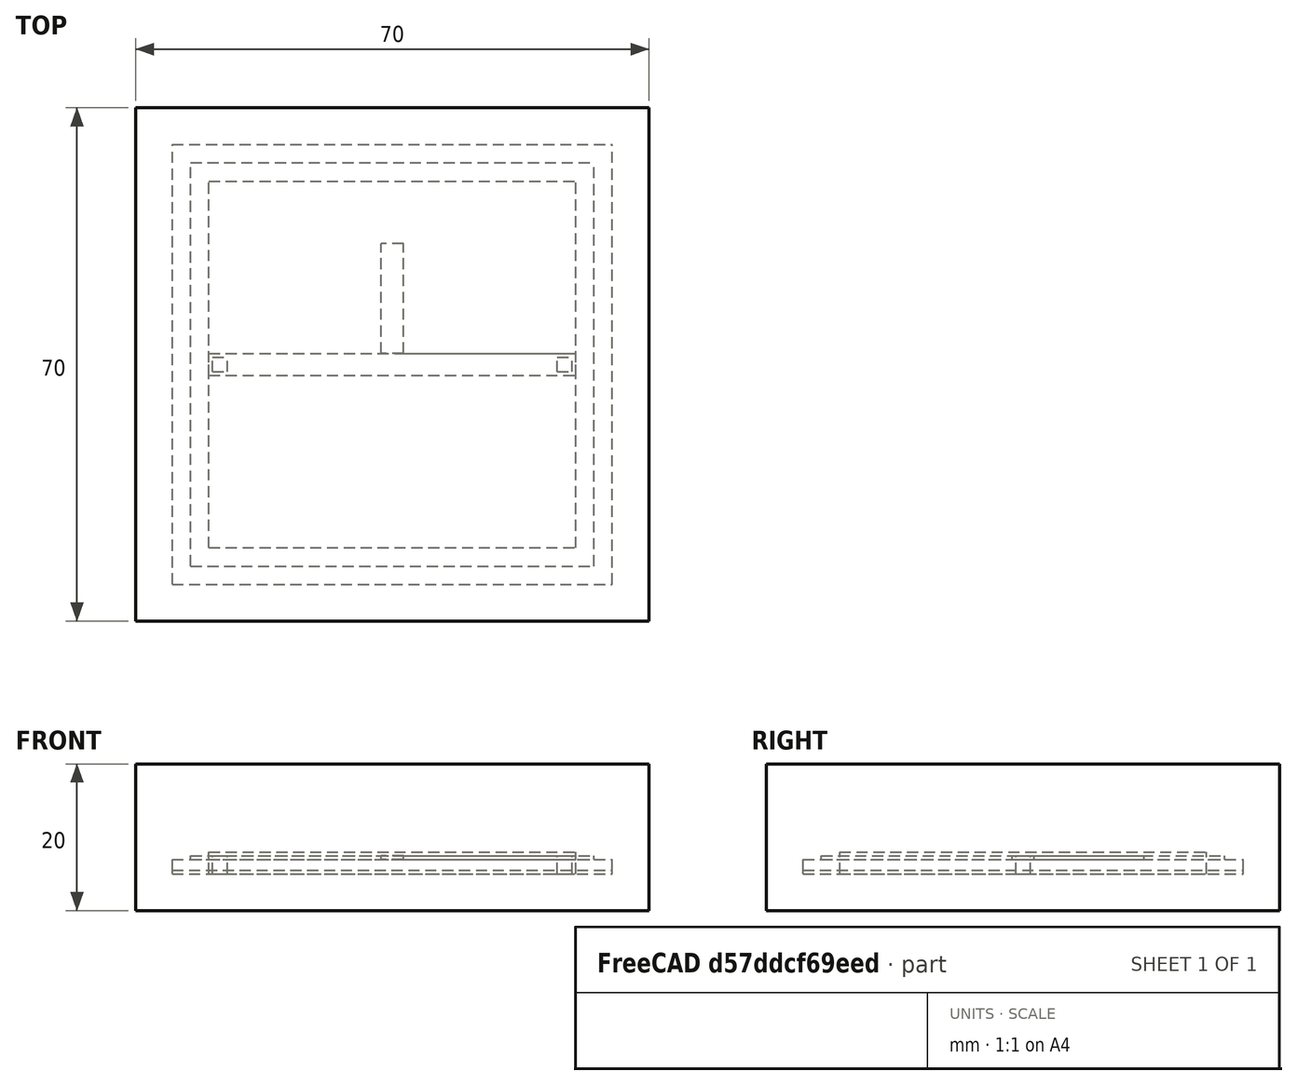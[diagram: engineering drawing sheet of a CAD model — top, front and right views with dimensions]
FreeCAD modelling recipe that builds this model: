
FCSTD DOCUMENT  (FreeCAD 0.21R29450 (Git))
Label: 002
License: All rights reserved
LicenseURL: http://en.wikipedia.org/wiki/All_rights_reserved
objects: Part::Box×9, PartDesign::Boolean×1, PartDesign::Body×1
note: 11 computed .brp shape members not serialized (recipe doc carries the construction recipe); baked Part::Feature solids carry a one-line shape summary decoded from their .brp

FEATURE [Part::Box] Box  label="Substrate"
  AttacherType = Attacher::AttachEngine3D
  Height = 1.5
  Length = 60
  Placement = pos=(-5,-5,0.5) rot=(0,0,1;0rad)
  Width = 60
FEATURE [Part::Box] Box001  label="GND"
  AttacherType = Attacher::AttachEngine3D
  Height = 0.5
  Length = 60
  Placement = pos=(-5,-5,0) rot=(0,0,1;0rad)
  Width = 60
FEATURE [Part::Box] Box002  label="Trace1"
  AttacherType = Attacher::AttachEngine3D
  Height = 0.5
  Length = 50
  Placement = pos=(0,23.5,2) rot=(0,0,1;0rad)
  Width = 3
FEATURE [Part::Box] Box003  label="Stub1"
  AttacherType = Attacher::AttachEngine3D
  Height = 0.5
  Length = 15
  Placement = pos=(26.5,26.5,2) rot=(0,0,1;1.5708rad)
  Width = 3
FEATURE [PartDesign::Boolean] Boolean
  Group = -> [Box002,Box003]
  Type = 0
FEATURE [PartDesign::Body] Body  label="Top_Conductor"
  Group = -> [Boolean]
  Origin = -> Origin
  Tip = -> Boolean
FEATURE [Part::Box] Box004  label="Term_IN"
  AttacherType = Attacher::AttachEngine3D
  Height = 2.5
  Length = 2
  Placement = pos=(0.5,24,0) rot=(0,0,1;0rad)
  Width = 2
FEATURE [Part::Box] Box005  label="Term_OUT"
  AttacherType = Attacher::AttachEngine3D
  Height = 2.5
  Length = 2
  Placement = pos=(47.5,24,0) rot=(0,0,1;0rad)
  Width = 2
FEATURE [Part::Box] Box006  label="Air_Volume"
  AttacherType = Attacher::AttachEngine3D
  Height = 20
  Length = 70
  Placement = pos=(-10,-10,-5) rot=(0,0,1;0rad)
  Width = 70
FEATURE [Part::Box] Box007  label="electric field port"
  AttacherType = Attacher::AttachEngine3D
  Height = 0.5
  Length = 55
  Placement = pos=(-2.5,-2.5,2) rot=(0,0,1;0rad)
  Width = 55
FEATURE [Part::Box] Box008  label="fine mesh region"
  AttacherType = Attacher::AttachEngine3D
  Height = 3
  Length = 50
  Width = 50
